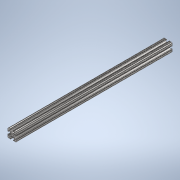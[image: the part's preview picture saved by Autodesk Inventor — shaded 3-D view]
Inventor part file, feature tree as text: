
AUTODESK INVENTOR PART (.ipt)
format: ipt  version: 2020 (Build 240168000, 168)  size: 239,616 bytes
history: native  units: in
note: dims shown in document units (in); Inventor stores cm internally (conversion verified against a paired STEP export)
features: extrude x1, sketch x1
ambient origin geometry x8: Origin, YZ Plane, XZ Plane, XY Plane, X Axis, Y Axis, Z Axis, Center Point
bodies: Solid1 (feature_tree)
feature tree (2):
  extrude  "Extrusion1"  [1 undecoded]
  sketch  "Sketch1"  dims[d0=18.0in d1=0.0in]
note: 1 required parameter value undecoded (feature->parameter linkage not recoverable at this tier; creation-order binding heuristic only, values carry confidence <= 0.55)
